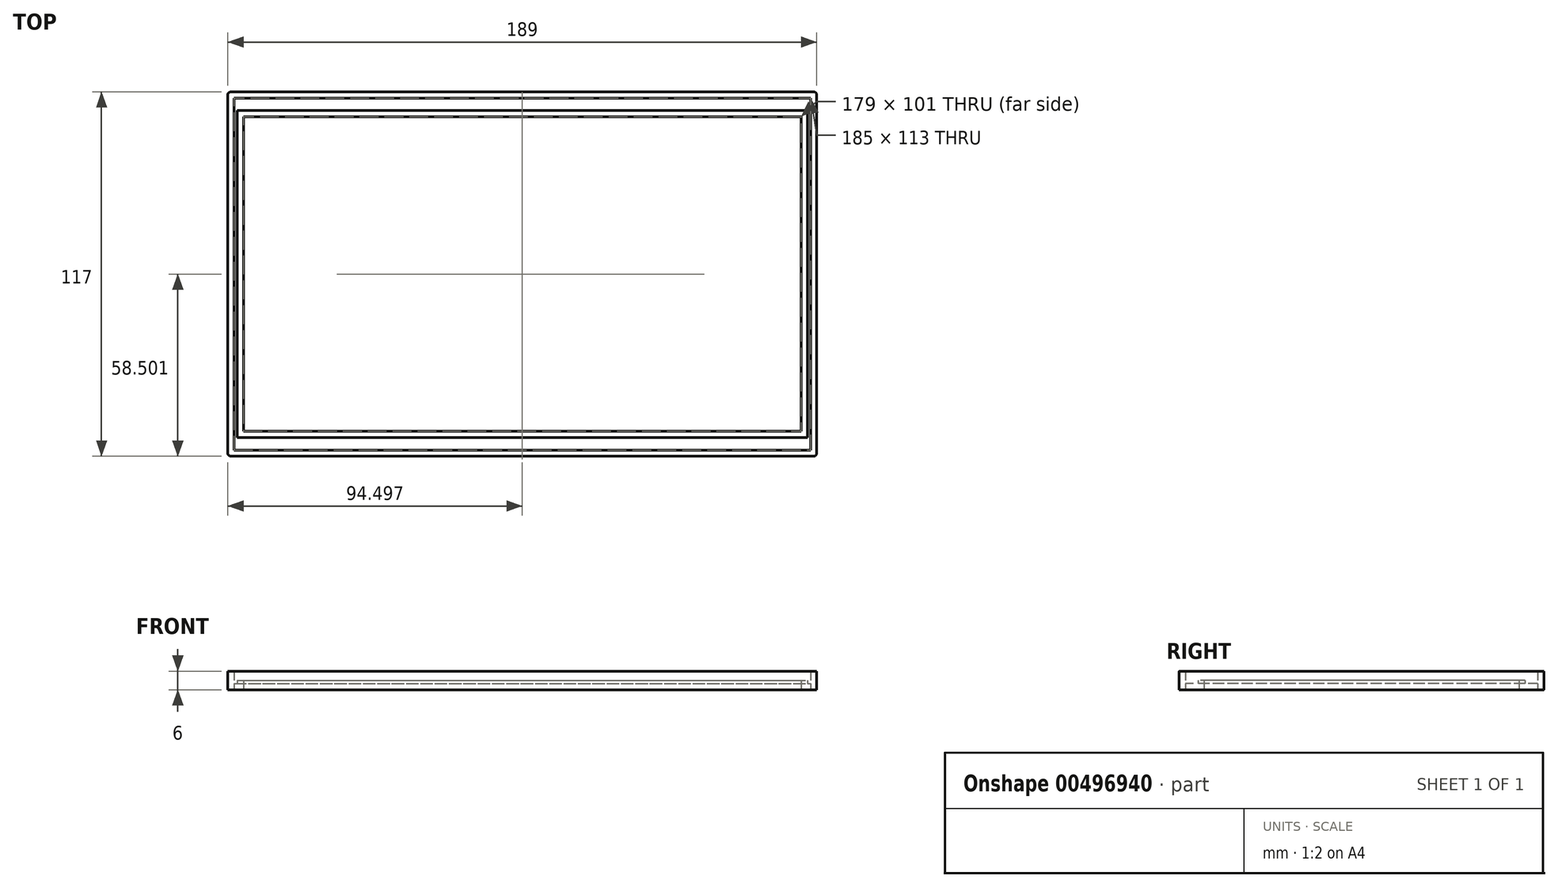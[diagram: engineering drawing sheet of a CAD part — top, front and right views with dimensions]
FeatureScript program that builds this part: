
annotation { "Feature Type Name" : "Feature", "Feature Type Description" : "" }
export const myFeature = defineFeature(function(context is Context, id is Id, definition is map)
    precondition{}
    {
        {
            var Q0;
            Q0=qCreatedBy(makeId("Top.planeOp"),FACE);
            var sketch = newSketch(context, id + "F0", { "sketchPlane" : qUnion([Q0])});
            skLineSegment(sketch, "E0.bottom", {"start": v(-96.4, 71.52) * mm, "end": v(92.6, 71.52) * mm});
            skLineSegment(sketch, "E0.top", {"start": v(-96.4, -45.48) * mm, "end": v(92.6, -45.48) * mm});
            skLineSegment(sketch, "E0.left", {"start": v(-96.4, 71.52) * mm, "end": v(-96.4, -45.48) * mm});
            skLineSegment(sketch, "E0.right", {"start": v(92.6, 71.52) * mm, "end": v(92.6, -45.48) * mm});
            skLineSegment(sketch, "E1.bottom", {"start": v(-91.4, 63.52) * mm, "end": v(87.6, 63.52) * mm});
            skLineSegment(sketch, "E1.top", {"start": v(-91.4, -37.48) * mm, "end": v(87.6, -37.48) * mm});
            skLineSegment(sketch, "E1.left", {"start": v(-91.4, 63.52) * mm, "end": v(-91.4, -37.48) * mm});
            skLineSegment(sketch, "E1.right", {"start": v(87.6, 63.52) * mm, "end": v(87.6, -37.48) * mm});
            skLineSegment(sketch, "E2.0", {"start": v(-93.4, 65.52) * mm, "end": v(89.6, 65.52) * mm});
            skLineSegment(sketch, "E2.1", {"start": v(-93.4, 65.52) * mm, "end": v(-93.4, -39.48) * mm});
            skLineSegment(sketch, "E2.2", {"start": v(-93.4, -39.48) * mm, "end": v(89.6, -39.48) * mm});
            skLineSegment(sketch, "E2.3", {"start": v(89.6, 65.52) * mm, "end": v(89.6, -39.48) * mm});
            skLineSegment(sketch, "E3.0", {"start": v(-94.4, 69.52) * mm, "end": v(90.6, 69.52) * mm});
            skLineSegment(sketch, "E3.1", {"start": v(-94.4, 69.52) * mm, "end": v(-94.4, -43.48) * mm});
            skLineSegment(sketch, "E3.2", {"start": v(-94.4, -43.48) * mm, "end": v(90.6, -43.48) * mm});
            skLineSegment(sketch, "E3.3", {"start": v(90.6, 69.52) * mm, "end": v(90.6, -43.48) * mm});
            skSolve(sketch);
        }
        {
            var Q0;
            Q0=makeQuery(id+"F0.imprint","IMPRINT",FACE,{"disambiguationData":[TD([[makeQuery(id+"F0.imprint","IMPRINT",EDGE,{"derivedFrom":sQuery(id+"F0.wireOp",EDGE,"E0.bottom")}),-1.0]])]});
            extrude(context, id + "F1", {"entities" : qUnion([Q0]), "depth" : 6 * mm});
        }
        {
            var Q0;
            Q0=makeQuery(id+"F0.imprint","IMPRINT",FACE,{"disambiguationData":[TD([[makeQuery(id+"F0.imprint","IMPRINT",EDGE,{"derivedFrom":sQuery(id+"F0.wireOp",EDGE,"E2.0")}),1.0]])]});
            extrude(context, id + "F2", {"entities" : qUnion([Q0]), "depth" : 2 * mm});
        }
        {
            var Q0;
            Q0=makeQuery(id+"F1.opExtrude","SWEPT_EDGE",EDGE,{"disambiguationData":[OSD([sQuery(id+"F0.wireOp",EDGE,"E0.top"),sQuery(id+"F0.wireOp",EDGE,"E0.left")])]});
            var Q1;
            Q1=makeQuery(id+"F1.opExtrude","SWEPT_EDGE",EDGE,{"disambiguationData":[OSD([sQuery(id+"F0.wireOp",EDGE,"E0.bottom"),sQuery(id+"F0.wireOp",EDGE,"E0.left")])]});
            var Q2;
            Q2=makeQuery(id+"F1.opExtrude","SWEPT_EDGE",EDGE,{"disambiguationData":[OSD([sQuery(id+"F0.wireOp",EDGE,"E0.bottom"),sQuery(id+"F0.wireOp",EDGE,"E0.right")])]});
            var Q3;
            Q3=makeQuery(id+"F1.opExtrude","SWEPT_EDGE",EDGE,{"disambiguationData":[OSD([sQuery(id+"F0.wireOp",EDGE,"E0.top"),sQuery(id+"F0.wireOp",EDGE,"E0.right")])]});
            fillet(context, id + "F3", {"entities" : qUnion([Q0, Q1, Q2, Q3]), "radius" : 1 * mm, "tangentPropagation" : true, "allowEdgeOverflow" : false});
        }
        {
            var Q0;
            Q0=makeQuery(id+"F0.imprint","IMPRINT",FACE,{"disambiguationData":[TD([[makeQuery(id+"F0.imprint","IMPRINT",EDGE,{"derivedFrom":sQuery(id+"F0.wireOp",EDGE,"E1.bottom")}),1.0]])]});
            extrude(context, id + "F4", {"entities" : qUnion([Q0]), "operationType" : NewBodyOperationType.ADD, "depth" : 3 * mm});
        }
    });
